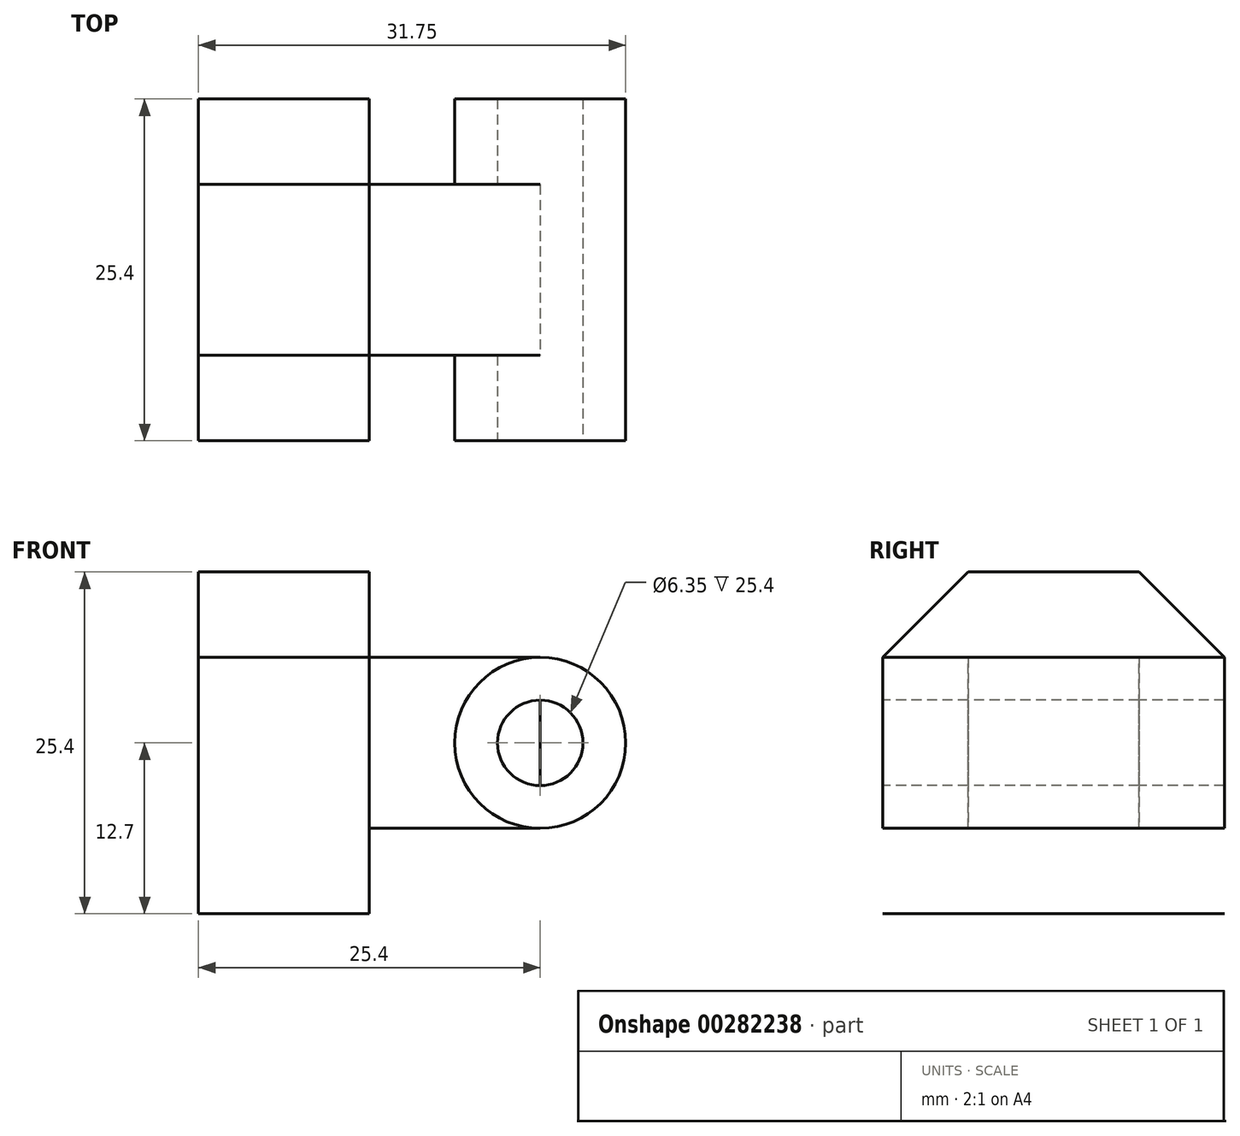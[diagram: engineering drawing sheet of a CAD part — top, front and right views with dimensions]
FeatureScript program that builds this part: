
annotation { "Feature Type Name" : "Feature", "Feature Type Description" : "" }
export const myFeature = defineFeature(function(context is Context, id is Id, definition is map)
    precondition{}
    {
        {
            var Q0;
            Q0=qCreatedBy(makeId("Front.planeOp"),FACE);
            var sketch = newSketch(context, id + "F0", { "sketchPlane" : qUnion([Q0])});
            skLineSegment(sketch, "E0.bottom", {"start": v(0, 0) * mm, "end": v(12.7, 0) * mm});
            skLineSegment(sketch, "E0.top", {"start": v(0, 25.4) * mm, "end": v(12.7, 25.4) * mm});
            skLineSegment(sketch, "E0.left", {"start": v(0, 0) * mm, "end": v(0, 25.4) * mm});
            skLineSegment(sketch, "E0.right", {"start": v(12.7, 0) * mm, "end": v(12.7, 25.4) * mm});
            skSolve(sketch);
        }
        {
            var Q0;
            Q0=makeQuery(id+"F0.imprint","IMPRINT",FACE,{"disambiguationData":[TD([[makeQuery(id+"F0.imprint","IMPRINT",EDGE,{"derivedFrom":sQuery(id+"F0.wireOp",EDGE,"E0.bottom")}),1.0]])]});
            extrude(context, id + "F1", {"entities" : qUnion([Q0]), "oppositeDirection" : true, "depth" : 25.4 * mm});
        }
        {
            var Q0;
            Q0=makeQuery(id+"F1.opExtrude","SWEPT_FACE",FACE,{"disambiguationData":[OSD([sQuery(id+"F0.wireOp",EDGE,"E0.right")])]});
            var sketch = newSketch(context, id + "F2", { "sketchPlane" : qUnion([Q0])});
            skLineSegment(sketch, "E1", {"start": v(0, 25.4) * mm, "end": v(6.35, 25.4) * mm});
            skLineSegment(sketch, "E2", {"start": v(6.35, 25.4) * mm, "end": v(0, 19.05) * mm});
            skLineSegment(sketch, "E3", {"start": v(0, 19.05) * mm, "end": v(0, 25.4) * mm});
            skLineSegment(sketch, "E4", {"start": v(25.4, 25.4) * mm, "end": v(19.05, 25.4) * mm});
            skLineSegment(sketch, "E5", {"start": v(19.05, 25.4) * mm, "end": v(25.4, 19.05) * mm});
            skLineSegment(sketch, "E6", {"start": v(25.4, 19.05) * mm, "end": v(25.4, 25.4) * mm});
            skSolve(sketch);
        }
        {
            var Q0;
            Q0=makeQuery(id+"F2.imprint","IMPRINT",FACE,{"disambiguationData":[TD([[makeQuery(id+"F2.imprint","IMPRINT",EDGE,{"derivedFrom":sQuery(id+"F2.wireOp",EDGE,"E1")}),1.0]])]});
            var Q1;
            Q1=makeQuery(id+"F2.imprint","IMPRINT",FACE,{"disambiguationData":[TD([[makeQuery(id+"F2.imprint","IMPRINT",EDGE,{"derivedFrom":sQuery(id+"F2.wireOp",EDGE,"E4")}),1.0]])]});
            extrude(context, id + "F3", {"entities" : qUnion([Q0, Q1]), "operationType" : NewBodyOperationType.REMOVE, "oppositeDirection" : true, "depth" : 12.7 * mm});
        }
        {
            var Q0;
            Q0=makeQuery(id+"F1.opExtrude","SWEPT_FACE",FACE,{"disambiguationData":[OSD([sQuery(id+"F0.wireOp",EDGE,"E0.right")])]});
            var sketch = newSketch(context, id + "F4", { "sketchPlane" : qUnion([Q0])});
            skLineSegment(sketch, "E7.bottom", {"start": v(6.35, 19.05) * mm, "end": v(19.05, 19.05) * mm});
            skLineSegment(sketch, "E7.top", {"start": v(6.35, 6.35) * mm, "end": v(19.05, 6.35) * mm});
            skLineSegment(sketch, "E7.left", {"start": v(6.35, 19.05) * mm, "end": v(6.35, 6.35) * mm});
            skLineSegment(sketch, "E7.right", {"start": v(19.05, 19.05) * mm, "end": v(19.05, 6.35) * mm});
            skSolve(sketch);
        }
        {
            var Q0;
            Q0=makeQuery(id+"F4.imprint","IMPRINT",FACE,{"disambiguationData":[TD([[makeQuery(id+"F4.imprint","IMPRINT",EDGE,{"derivedFrom":sQuery(id+"F4.wireOp",EDGE,"E7.bottom")}),-1.0]])]});
            extrude(context, id + "F5", {"entities" : qUnion([Q0]), "operationType" : NewBodyOperationType.ADD, "depth" : 12.7 * mm});
        }
        {
            var Q0;
            Q0=qCreatedBy(makeId("Front.planeOp"),FACE);
            var sketch = newSketch(context, id + "F6", { "sketchPlane" : qUnion([Q0])});
            skCircle(sketch, "E8", {"center": v(25.4, 12.7) * mm, "radius": 6.35 * mm});
            skCircle(sketch, "E9", {"center": v(25.4, 12.7) * mm, "radius": 3.18 * mm});
            skSolve(sketch);
        }
        {
            var Q0;
            Q0=makeQuery(id+"F6.imprint","IMPRINT",FACE,{"disambiguationData":[TD([[makeQuery(id+"F6.imprint","IMPRINT",EDGE,{"derivedFrom":sQuery(id+"F6.wireOp",EDGE,"E8")}),1.0]])]});
            extrude(context, id + "F7", {"entities" : qUnion([Q0]), "operationType" : NewBodyOperationType.ADD, "oppositeDirection" : true, "depth" : 25.4 * mm});
        }
    });
